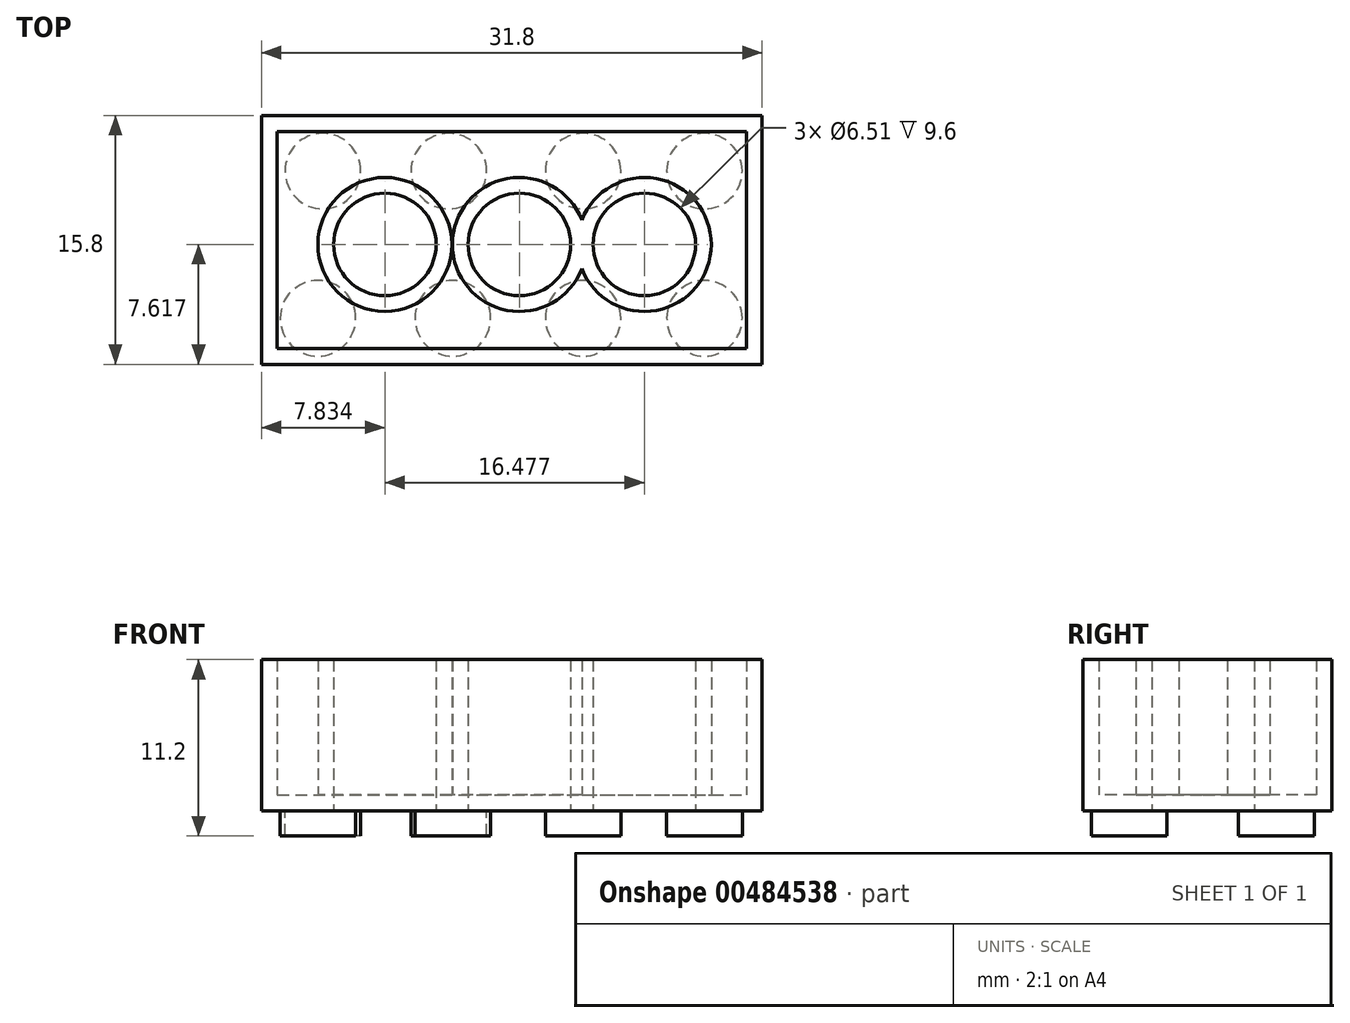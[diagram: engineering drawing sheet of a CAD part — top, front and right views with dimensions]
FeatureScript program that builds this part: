
annotation { "Feature Type Name" : "Feature", "Feature Type Description" : "" }
export const myFeature = defineFeature(function(context is Context, id is Id, definition is map)
    precondition{}
    {
        {
            var Q0;
            Q0=qCreatedBy(makeId("Top.planeOp"),FACE);
            var sketch = newSketch(context, id + "F0", { "sketchPlane" : qUnion([Q0])});
            skLineSegment(sketch, "E0.bottom", {"start": v(-107.44, 32.91) * mm, "end": v(-75.64, 32.91) * mm});
            skLineSegment(sketch, "E0.top", {"start": v(-107.44, 17.11) * mm, "end": v(-75.64, 17.11) * mm});
            skLineSegment(sketch, "E0.left", {"start": v(-107.44, 32.91) * mm, "end": v(-107.44, 17.11) * mm});
            skLineSegment(sketch, "E0.right", {"start": v(-75.64, 32.91) * mm, "end": v(-75.64, 17.11) * mm});
            skCircle(sketch, "E1", {"center": v(-103.54, 29.39) * mm, "radius": 2.4 * mm});
            skCircle(sketch, "E2", {"center": v(-103.85, 20.04) * mm, "radius": 2.4 * mm});
            skCircle(sketch, "E3", {"center": v(-95.54, 29.39) * mm, "radius": 2.4 * mm});
            skCircle(sketch, "E4", {"center": v(-95.3, 20.04) * mm, "radius": 2.4 * mm});
            skCircle(sketch, "E5", {"center": v(-87, 20.04) * mm, "radius": 2.4 * mm});
            skCircle(sketch, "E6", {"center": v(-79.3, 20.04) * mm, "radius": 2.4 * mm});
            skCircle(sketch, "E7", {"center": v(-79.3, 29.39) * mm, "radius": 2.4 * mm});
            skCircle(sketch, "E8", {"center": v(-87, 29.39) * mm, "radius": 2.4 * mm});
            skCircle(sketch, "E9", {"center": v(-99.6, 24.73) * mm, "radius": 3.25 * mm});
            skCircle(sketch, "E10", {"center": v(-91.06, 24.73) * mm, "radius": 3.25 * mm});
            skCircle(sketch, "E11", {"center": v(-83.13, 24.73) * mm, "radius": 3.25 * mm});
            skSolve(sketch);
        }
        {
            var Q0;
            Q0=makeQuery(id+"F0.imprint","IMPRINT",FACE,{"disambiguationData":[TD([[makeQuery(id+"F0.imprint","IMPRINT",EDGE,{"derivedFrom":sQuery(id+"F0.wireOp",EDGE,"E1")}),1.0]])]});
            var Q1;
            Q1=makeQuery(id+"F0.imprint","IMPRINT",FACE,{"disambiguationData":[TD([[makeQuery(id+"F0.imprint","IMPRINT",EDGE,{"derivedFrom":sQuery(id+"F0.wireOp",EDGE,"E7")}),1.0]])]});
            var Q2;
            Q2=makeQuery(id+"F0.imprint","IMPRINT",FACE,{"disambiguationData":[TD([[makeQuery(id+"F0.imprint","IMPRINT",EDGE,{"derivedFrom":sQuery(id+"F0.wireOp",EDGE,"E8")}),1.0]])]});
            var Q3;
            Q3=makeQuery(id+"F0.imprint","IMPRINT",FACE,{"disambiguationData":[TD([[makeQuery(id+"F0.imprint","IMPRINT",EDGE,{"derivedFrom":sQuery(id+"F0.wireOp",EDGE,"E0.bottom")}),-1.0]])]});
            var Q4;
            Q4=makeQuery(id+"F0.imprint","IMPRINT",FACE,{"disambiguationData":[TD([[makeQuery(id+"F0.imprint","IMPRINT",EDGE,{"derivedFrom":sQuery(id+"F0.wireOp",EDGE,"E6")}),1.0]])]});
            var Q5;
            Q5=makeQuery(id+"F0.imprint","IMPRINT",FACE,{"disambiguationData":[TD([[makeQuery(id+"F0.imprint","IMPRINT",EDGE,{"derivedFrom":sQuery(id+"F0.wireOp",EDGE,"E2")}),1.0]])]});
            var Q6;
            Q6=makeQuery(id+"F0.imprint","IMPRINT",FACE,{"disambiguationData":[TD([[makeQuery(id+"F0.imprint","IMPRINT",EDGE,{"derivedFrom":sQuery(id+"F0.wireOp",EDGE,"E3")}),1.0]])]});
            var Q7;
            Q7=makeQuery(id+"F0.imprint","IMPRINT",FACE,{"disambiguationData":[TD([[makeQuery(id+"F0.imprint","IMPRINT",EDGE,{"derivedFrom":sQuery(id+"F0.wireOp",EDGE,"E4")}),1.0]])]});
            var Q8;
            Q8=makeQuery(id+"F0.imprint","IMPRINT",FACE,{"disambiguationData":[TD([[makeQuery(id+"F0.imprint","IMPRINT",EDGE,{"derivedFrom":sQuery(id+"F0.wireOp",EDGE,"E5")}),1.0]])]});
            var Q9;
            {var subQ0=sQuery(id+"F0.wireOp",EDGE,"E9");var subQ1=sQuery(id+"F0.wireOp",EDGE,"E2");var subQ2=makeQuery(id+"F0.imprint","INTERSECT",VERTEX,{"disambiguationData":[OD(0.0)],"derivedFrom":[subQ1,subQ0]});Q9=makeQuery(id+"F0.imprint","IMPRINT",FACE,{"disambiguationData":[TD([[makeQuery(id+"F0.imprint","IMPRINT",EDGE,{"disambiguationData":[TD([[subQ2,-1.0]])],"derivedFrom":subQ1}),-1.0]])]});}
            var Q10;
            {var subQ0=sQuery(id+"F0.wireOp",EDGE,"E11");var subQ4=sQuery(id+"F0.wireOp",EDGE,"E5");var subQ5=makeQuery(id+"F0.imprint","INTERSECT",VERTEX,{"disambiguationData":[OD(0.0)],"derivedFrom":[subQ4,subQ0]});Q10=makeQuery(id+"F0.imprint","IMPRINT",FACE,{"disambiguationData":[TD([[makeQuery(id+"F0.imprint","IMPRINT",EDGE,{"disambiguationData":[TD([[subQ5,1.0]])],"derivedFrom":subQ4}),-1.0]])]});}
            var Q11;
            {var subQ0=sQuery(id+"F0.wireOp",EDGE,"E9");var subQ1=sQuery(id+"F0.wireOp",EDGE,"E4");var subQ2=makeQuery(id+"F0.imprint","INTERSECT",VERTEX,{"disambiguationData":[OD(0.0)],"derivedFrom":[subQ1,subQ0]});Q11=makeQuery(id+"F0.imprint","IMPRINT",FACE,{"disambiguationData":[TD([[makeQuery(id+"F0.imprint","IMPRINT",EDGE,{"disambiguationData":[TD([[subQ2,-1.0]])],"derivedFrom":subQ1}),1.0]])]});}
            var Q12;
            {var subQ0=sQuery(id+"F0.wireOp",EDGE,"E10");var subQ1=sQuery(id+"F0.wireOp",EDGE,"E4");var subQ2=makeQuery(id+"F0.imprint","INTERSECT",VERTEX,{"disambiguationData":[OD(0.0)],"derivedFrom":[subQ1,subQ0]});Q12=makeQuery(id+"F0.imprint","IMPRINT",FACE,{"disambiguationData":[TD([[makeQuery(id+"F0.imprint","IMPRINT",EDGE,{"disambiguationData":[TD([[subQ2,1.0]])],"derivedFrom":subQ1}),-1.0]])]});}
            var Q13;
            {var subQ0=sQuery(id+"F0.wireOp",EDGE,"E10");var subQ1=sQuery(id+"F0.wireOp",EDGE,"E4");var subQ2=makeQuery(id+"F0.imprint","INTERSECT",VERTEX,{"disambiguationData":[OD(0.0)],"derivedFrom":[subQ1,subQ0]});Q13=makeQuery(id+"F0.imprint","IMPRINT",FACE,{"disambiguationData":[TD([[makeQuery(id+"F0.imprint","IMPRINT",EDGE,{"disambiguationData":[TD([[subQ2,1.0]])],"derivedFrom":subQ1}),1.0]])]});}
            extrude(context, id + "F1", {"entities" : qUnion([Q0, Q1, Q2, Q3, Q4, Q5, Q6, Q7, Q8, Q9, Q10, Q11, Q12, Q13]), "depth" : 9.6 * mm});
        }
        {
            var Q0;
            Q0=makeQuery(id+"F0.imprint","IMPRINT",FACE,{"disambiguationData":[TD([[makeQuery(id+"F0.imprint","IMPRINT",EDGE,{"derivedFrom":sQuery(id+"F0.wireOp",EDGE,"E1")}),1.0]])]});
            var Q1;
            Q1=makeQuery(id+"F0.imprint","IMPRINT",FACE,{"disambiguationData":[TD([[makeQuery(id+"F0.imprint","IMPRINT",EDGE,{"derivedFrom":sQuery(id+"F0.wireOp",EDGE,"E8")}),1.0]])]});
            var Q2;
            Q2=makeQuery(id+"F0.imprint","IMPRINT",FACE,{"disambiguationData":[TD([[makeQuery(id+"F0.imprint","IMPRINT",EDGE,{"derivedFrom":sQuery(id+"F0.wireOp",EDGE,"E3")}),1.0]])]});
            var Q3;
            Q3=makeQuery(id+"F0.imprint","IMPRINT",FACE,{"disambiguationData":[TD([[makeQuery(id+"F0.imprint","IMPRINT",EDGE,{"derivedFrom":sQuery(id+"F0.wireOp",EDGE,"E7")}),1.0]])]});
            var Q4;
            Q4=makeQuery(id+"F0.imprint","IMPRINT",FACE,{"disambiguationData":[TD([[makeQuery(id+"F0.imprint","IMPRINT",EDGE,{"derivedFrom":sQuery(id+"F0.wireOp",EDGE,"E5")}),1.0]])]});
            var Q5;
            Q5=makeQuery(id+"F0.imprint","IMPRINT",FACE,{"disambiguationData":[TD([[makeQuery(id+"F0.imprint","IMPRINT",EDGE,{"derivedFrom":sQuery(id+"F0.wireOp",EDGE,"E6")}),1.0]])]});
            var Q6;
            Q6=makeQuery(id+"F0.imprint","IMPRINT",FACE,{"disambiguationData":[TD([[makeQuery(id+"F0.imprint","IMPRINT",EDGE,{"derivedFrom":sQuery(id+"F0.wireOp",EDGE,"E4")}),1.0]])]});
            var Q7;
            Q7=makeQuery(id+"F0.imprint","IMPRINT",FACE,{"disambiguationData":[TD([[makeQuery(id+"F0.imprint","IMPRINT",EDGE,{"derivedFrom":sQuery(id+"F0.wireOp",EDGE,"E2")}),1.0]])]});
            extrude(context, id + "F2", {"entities" : qUnion([Q0, Q1, Q2, Q3, Q4, Q5, Q6, Q7]), "oppositeDirection" : true, "depth" : 1.6 * mm});
        }
        {
            var Q0;
            Q0=makeQuery(id+"F1.opExtrude","CAP_FACE",FACE,{"disambiguationData":[OSD([sQuery(id+"F0.wireOp",EDGE,"E0.bottom"),sQuery(id+"F0.wireOp",EDGE,"E0.top"),sQuery(id+"F0.wireOp",EDGE,"E0.left"),sQuery(id+"F0.wireOp",EDGE,"E0.right"),sQuery(id+"F0.wireOp",EDGE,"E9"),sQuery(id+"F0.wireOp",EDGE,"E10"),sQuery(id+"F0.wireOp",EDGE,"E11")])],"isStart":false});
            shell(context, id + "F3", {"entities" : qUnion([Q0]), "thickness" : 1 * mm});
        }
    });
